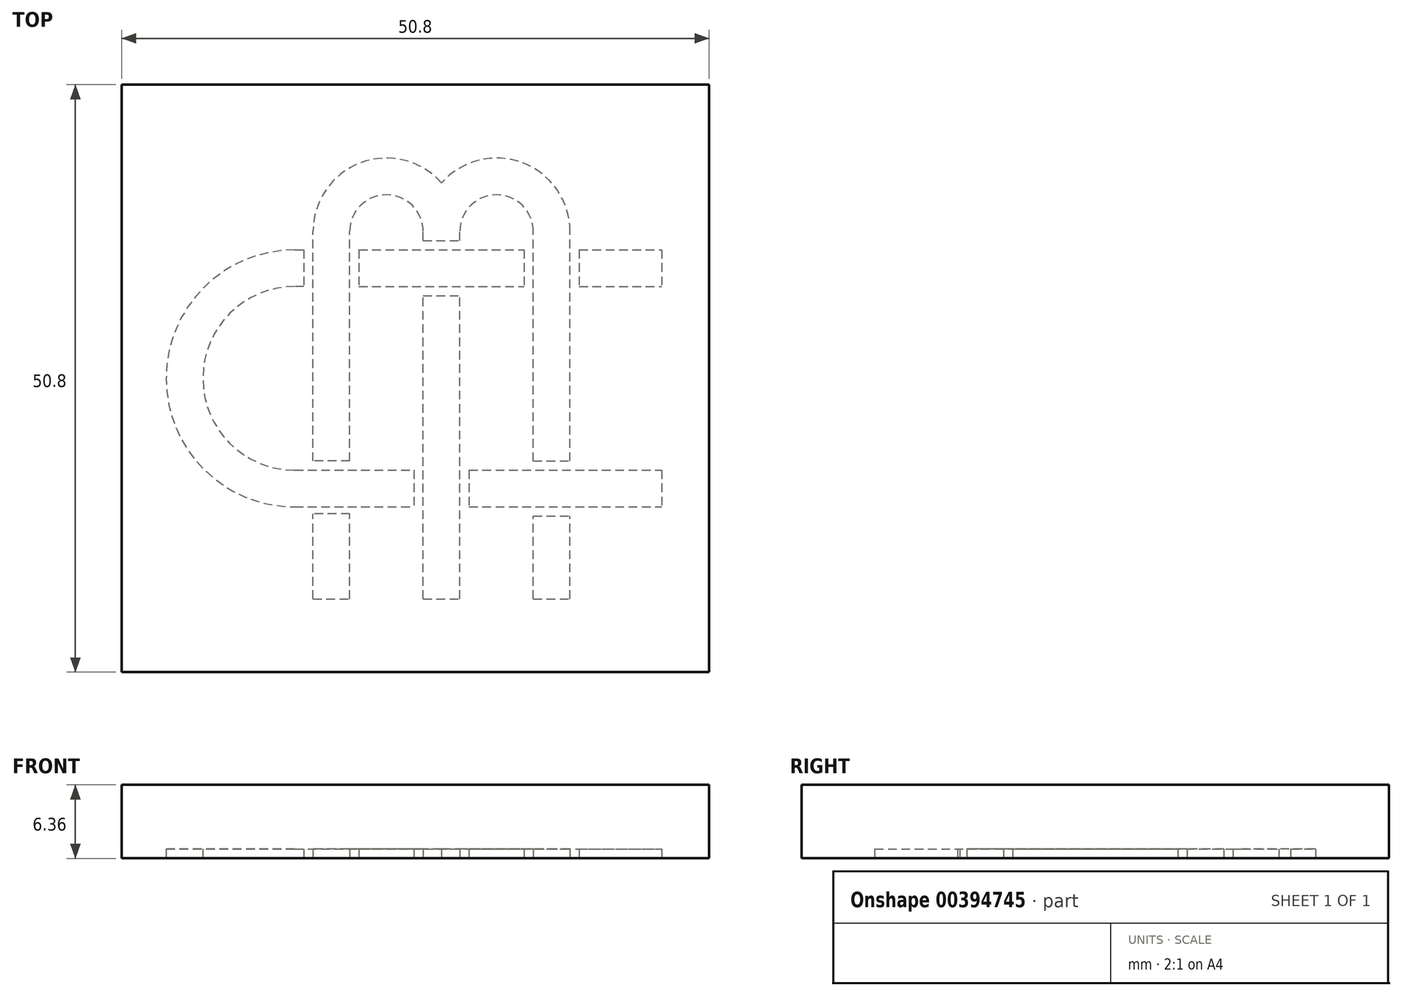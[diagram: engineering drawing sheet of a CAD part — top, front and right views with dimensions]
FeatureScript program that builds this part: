
annotation { "Feature Type Name" : "Feature", "Feature Type Description" : "" }
export const myFeature = defineFeature(function(context is Context, id is Id, definition is map)
    precondition{}
    {
        {
            var Q0;
            Q0=qCreatedBy(makeId("Top.planeOp"),FACE);
            var sketch = newSketch(context, id + "F0", { "sketchPlane" : qUnion([Q0])});
            skLineSegment(sketch, "E0.bottom", {"start": v(0, 0) * mm, "end": v(50.8, 0) * mm});
            skLineSegment(sketch, "E0.top", {"start": v(0, 50.8) * mm, "end": v(50.8, 50.8) * mm});
            skLineSegment(sketch, "E0.left", {"start": v(0, 0) * mm, "end": v(0, 50.8) * mm});
            skLineSegment(sketch, "E0.right", {"start": v(50.8, 0) * mm, "end": v(50.8, 50.8) * mm});
            skSolve(sketch);
        }
        {
            var Q0;
            Q0 = qSketchRegion(id + "F0", true);
            extrude(context, id + "F1", {"entities" : qUnion([Q0]), "depth" : 3.17 * mm});
        }
        {
            var Q0;
            Q0=makeQuery(id+"F1.opExtrude","CAP_FACE",FACE,{"disambiguationData":[OSD([sQuery(id+"F0.wireOp",EDGE,"E0.bottom"),sQuery(id+"F0.wireOp",EDGE,"E0.top"),sQuery(id+"F0.wireOp",EDGE,"E0.left"),sQuery(id+"F0.wireOp",EDGE,"E0.right")])],"isStart":false});
            var sketch = newSketch(context, id + "F2", { "sketchPlane" : qUnion([Q0])});
            skLineSegment(sketch, "E1.bottom", {"start": v(19.72, 12.7) * mm, "end": v(16.55, 12.7) * mm});
            skLineSegment(sketch, "E1.left", {"start": v(19.72, 12.7) * mm, "end": v(19.72, 13.7) * mm});
            skLineSegment(sketch, "E1.right", {"start": v(16.55, 12.7) * mm, "end": v(16.55, 13.7) * mm});
            skLineSegment(sketch, "E2", {"start": v(16.55, 12.7) * mm, "end": v(54.65, 12.7) * mm, "construction": true});
            skLineSegment(sketch, "E3.bottom", {"start": v(26.07, 12.7) * mm, "end": v(29.25, 12.7) * mm});
            skLineSegment(sketch, "E3.left", {"start": v(26.07, 12.7) * mm, "end": v(26.07, 32.6) * mm});
            skLineSegment(sketch, "E3.right", {"start": v(29.25, 12.7) * mm, "end": v(29.25, 32.6) * mm});
            skLineSegment(sketch, "E4.bottom", {"start": v(35.6, 12.7) * mm, "end": v(38.77, 12.7) * mm});
            skLineSegment(sketch, "E4.left", {"start": v(35.6, 12.7) * mm, "end": v(35.6, 13.5) * mm});
            skLineSegment(sketch, "E4.right", {"start": v(38.77, 12.7) * mm, "end": v(38.77, 13.5) * mm});
            skLineSegment(sketch, "E5.0", {"start": v(50.8, 0) * mm, "end": v(50.8, 50.8) * mm, "construction": true});
            skLineSegment(sketch, "E6", {"start": v(11.9, 41.28) * mm, "end": v(43.43, 41.28) * mm, "construction": true});
            skLineSegment(sketch, "E7", {"start": v(22.9, 41.28) * mm, "end": v(22.9, 12.7) * mm, "construction": true});
            skLineSegment(sketch, "E8", {"start": v(32.42, 41.28) * mm, "end": v(32.42, 12.7) * mm, "construction": true});
            skLineSegment(sketch, "E9", {"start": v(27.66, 41.28) * mm, "end": v(27.66, 34.87) * mm, "construction": true});
            skLineSegment(sketch, "E10", {"start": v(19.72, 38.1) * mm, "end": v(26.07, 38.1) * mm, "construction": true});
            skLineSegment(sketch, "E11", {"start": v(29.25, 38.1) * mm, "end": v(35.6, 38.1) * mm, "construction": true});
            skArc(sketch, "E12", {"start": v(19.72, 38.1) * mm, "mid": v(22.9, 41.28) * mm, "end": v(26.07, 38.1) * mm});
            skArc(sketch, "E13", {"start": v(29.25, 38.1) * mm, "mid": v(32.42, 41.28) * mm, "end": v(35.6, 38.1) * mm});
            skCircle(sketch, "E14", {"center": v(22.9, 38.1) * mm, "radius": 6.35 * mm, "construction": true});
            skCircle(sketch, "E15", {"center": v(32.42, 38.1) * mm, "radius": 6.35 * mm, "construction": true});
            skArc(sketch, "E16", {"start": v(16.55, 38.1) * mm, "mid": v(20.65, 44.04) * mm, "end": v(27.66, 42.3) * mm});
            skArc(sketch, "E17", {"start": v(38.77, 38.1) * mm, "mid": v(34.67, 44.04) * mm, "end": v(27.66, 42.3) * mm});
            skLineSegment(sketch, "E18", {"start": v(22.9, 31.75) * mm, "end": v(42, 31.75) * mm, "construction": true});
            skLineSegment(sketch, "E19", {"start": v(22.9, 31.75) * mm, "end": v(16.55, 31.75) * mm, "construction": true});
            skLineSegment(sketch, "E20.0", {"start": v(0, 50.8) * mm, "end": v(50.8, 50.8) * mm, "construction": true});
            skLineSegment(sketch, "E21", {"start": v(0, 14.29) * mm, "end": v(50.8, 14.29) * mm, "construction": true});
            skLineSegment(sketch, "E22", {"start": v(0, 36.51) * mm, "end": v(50.8, 36.51) * mm, "construction": true});
            skLineSegment(sketch, "E23", {"start": v(0, 25.4) * mm, "end": v(50.8, 25.4) * mm, "construction": true});
            skLineSegment(sketch, "E24", {"start": v(0, 33.34) * mm, "end": v(50.8, 33.34) * mm, "construction": true});
            skLineSegment(sketch, "E25", {"start": v(0, 17.46) * mm, "end": v(50.8, 17.46) * mm, "construction": true});
            skLineSegment(sketch, "E26", {"start": v(14.96, 36.51) * mm, "end": v(14.96, 33.34) * mm, "construction": true});
            skLineSegment(sketch, "E27", {"start": v(14.96, 17.46) * mm, "end": v(14.96, 14.29) * mm, "construction": true});
            skLineSegment(sketch, "E28", {"start": v(8.61, 36.51) * mm, "end": v(8.61, 14.29) * mm, "construction": true});
            skLineSegment(sketch, "E29", {"start": v(8.61, 25.4) * mm, "end": v(11.79, 25.4) * mm, "construction": true});
            skLineSegment(sketch, "E30", {"start": v(15.75, 36.51) * mm, "end": v(15.75, 33.34) * mm, "construction": true});
            skLineSegment(sketch, "E31", {"start": v(14.96, 36.51) * mm, "end": v(15.75, 36.51) * mm});
            skLineSegment(sketch, "E32", {"start": v(15.75, 33.34) * mm, "end": v(14.96, 33.34) * mm});
            skLineSegment(sketch, "E33", {"start": v(15.75, 36.51) * mm, "end": v(15.75, 33.34) * mm});
            skLineSegment(sketch, "E34", {"start": v(26.07, 32.54) * mm, "end": v(29.25, 32.54) * mm});
            skLineSegment(sketch, "E35", {"start": v(26.07, 37.3) * mm, "end": v(29.25, 37.3) * mm});
            skLineSegment(sketch, "E36.trimOffspring", {"start": v(26.07, 37.3) * mm, "end": v(26.07, 38.1) * mm});
            skLineSegment(sketch, "E37.trimOffspring", {"start": v(29.25, 37.3) * mm, "end": v(29.25, 38.1) * mm});
            skLineSegment(sketch, "E38", {"start": v(20.52, 36.51) * mm, "end": v(20.52, 33.34) * mm});
            skLineSegment(sketch, "E39", {"start": v(34.8, 36.51) * mm, "end": v(34.8, 33.34) * mm});
            skLineSegment(sketch, "E40", {"start": v(20.52, 36.51) * mm, "end": v(34.8, 36.51) * mm});
            skLineSegment(sketch, "E41", {"start": v(20.52, 33.34) * mm, "end": v(34.8, 33.34) * mm});
            skLineSegment(sketch, "E42", {"start": v(39.57, 36.51) * mm, "end": v(39.57, 33.34) * mm});
            skLineSegment(sketch, "E43", {"start": v(39.57, 36.51) * mm, "end": v(40.36, 36.51) * mm});
            skLineSegment(sketch, "E44", {"start": v(39.57, 33.34) * mm, "end": v(40.36, 33.34) * mm});
            skLineSegment(sketch, "E45", {"start": v(19.72, 18.26) * mm, "end": v(16.55, 18.26) * mm});
            skLineSegment(sketch, "E46", {"start": v(19.72, 13.7) * mm, "end": v(16.55, 13.7) * mm});
            skLineSegment(sketch, "E47.trimOffspring", {"start": v(16.55, 18.26) * mm, "end": v(16.55, 38.1) * mm});
            skLineSegment(sketch, "E48.trimOffspring", {"start": v(19.72, 18.26) * mm, "end": v(19.72, 38.1) * mm});
            skLineSegment(sketch, "E49", {"start": v(25.28, 17.46) * mm, "end": v(25.28, 14.29) * mm});
            skLineSegment(sketch, "E50", {"start": v(14.96, 17.46) * mm, "end": v(25.28, 17.46) * mm});
            skLineSegment(sketch, "E51", {"start": v(14.96, 14.29) * mm, "end": v(25.28, 14.29) * mm});
            skLineSegment(sketch, "E52", {"start": v(35.6, 18.26) * mm, "end": v(38.77, 18.26) * mm});
            skLineSegment(sketch, "E53", {"start": v(35.6, 13.5) * mm, "end": v(38.77, 13.5) * mm});
            skLineSegment(sketch, "E54.trimOffspring", {"start": v(35.6, 18.26) * mm, "end": v(35.6, 38.1) * mm});
            skLineSegment(sketch, "E55.trimOffspring", {"start": v(38.77, 18.26) * mm, "end": v(38.77, 38.1) * mm});
            skLineSegment(sketch, "E56", {"start": v(30.04, 17.46) * mm, "end": v(30.04, 14.29) * mm});
            skLineSegment(sketch, "E57", {"start": v(30.04, 17.46) * mm, "end": v(40.36, 17.46) * mm});
            skLineSegment(sketch, "E58", {"start": v(30.04, 14.29) * mm, "end": v(40.36, 14.29) * mm});
            skLineSegment(sketch, "E59", {"start": v(46.71, 14.29) * mm, "end": v(46.71, 36.51) * mm, "construction": true});
            skLineSegment(sketch, "E60", {"start": v(40.36, 36.51) * mm, "end": v(46.71, 36.51) * mm});
            skLineSegment(sketch, "E61", {"start": v(46.71, 33.34) * mm, "end": v(40.36, 33.34) * mm});
            skLineSegment(sketch, "E62", {"start": v(40.36, 17.46) * mm, "end": v(46.71, 17.46) * mm});
            skLineSegment(sketch, "E63", {"start": v(46.71, 17.46) * mm, "end": v(46.71, 14.29) * mm});
            skLineSegment(sketch, "E64", {"start": v(39.57, 36.51) * mm, "end": v(46.71, 36.51) * mm});
            skLineSegment(sketch, "E65", {"start": v(46.71, 36.51) * mm, "end": v(46.71, 33.34) * mm});
            skLineSegment(sketch, "E66.bottom", {"start": v(30.04, 17.46) * mm, "end": v(46.71, 17.46) * mm});
            skLineSegment(sketch, "E66.top", {"start": v(30.04, 17.46) * mm, "end": v(46.71, 17.46) * mm});
            skLineSegment(sketch, "E66.left", {"start": v(30.04, 17.46) * mm, "end": v(30.04, 17.46) * mm});
            skLineSegment(sketch, "E66.right", {"start": v(46.71, 17.46) * mm, "end": v(46.71, 17.46) * mm});
            skLineSegment(sketch, "E67", {"start": v(30.04, 14.29) * mm, "end": v(46.71, 14.29) * mm});
            skLineSegment(sketch, "E68.bottom", {"start": v(16.55, 12.7) * mm, "end": v(19.72, 12.7) * mm});
            skLineSegment(sketch, "E68.top", {"start": v(16.55, 6.33) * mm, "end": v(19.72, 6.33) * mm});
            skLineSegment(sketch, "E68.left", {"start": v(16.55, 12.7) * mm, "end": v(16.55, 6.33) * mm});
            skLineSegment(sketch, "E68.right", {"start": v(19.72, 12.7) * mm, "end": v(19.72, 6.33) * mm});
            skPoint(sketch, "E69.oppositeSnap0", {"position": v(18.14, 6.33) * mm});
            skLineSegment(sketch, "E69.top", {"start": v(35.6, 6.33) * mm, "end": v(38.77, 6.33) * mm});
            skLineSegment(sketch, "E69.left", {"start": v(35.6, 12.7) * mm, "end": v(35.6, 6.33) * mm});
            skLineSegment(sketch, "E69.right", {"start": v(38.77, 12.7) * mm, "end": v(38.77, 6.33) * mm});
            skLineSegment(sketch, "E70.top", {"start": v(26.07, 6.33) * mm, "end": v(29.25, 6.33) * mm});
            skLineSegment(sketch, "E70.left", {"start": v(26.07, 12.7) * mm, "end": v(26.07, 6.33) * mm});
            skLineSegment(sketch, "E70.right", {"start": v(29.25, 12.7) * mm, "end": v(29.25, 6.33) * mm});
            skLineSegment(sketch, "E71.0", {"start": v(0, 0) * mm, "end": v(50.8, 0) * mm, "construction": true});
            skLineSegment(sketch, "E72", {"start": v(14.96, 33.34) * mm, "end": v(14.96, 17.46) * mm, "construction": true});
            skArc(sketch, "E73", {"start": v(14.96, 17.46) * mm, "mid": v(7.02, 25.4) * mm, "end": v(14.96, 33.34) * mm});
            skArc(sketch, "E74", {"start": v(14.96, 14.29) * mm, "mid": v(3.85, 25.4) * mm, "end": v(14.96, 36.51) * mm});
            skLineSegment(sketch, "E75.0", {"start": v(0, 0) * mm, "end": v(0, 50.8) * mm, "construction": true});
            skSolve(sketch);
        }
        {
            var Q0;
            Q0 = qSketchRegion(id + "F2", true);
            extrude(context, id + "F3", {"entities" : qUnion([Q0]), "operationType" : NewBodyOperationType.ADD, "depth" : 0.8 * mm});
        }
        {
            var Q0;
            Q0=makeQuery(id+"F1.opExtrude","CAP_FACE",FACE,{"disambiguationData":[OSD([sQuery(id+"F0.wireOp",EDGE,"E0.bottom"),sQuery(id+"F0.wireOp",EDGE,"E0.top"),sQuery(id+"F0.wireOp",EDGE,"E0.left"),sQuery(id+"F0.wireOp",EDGE,"E0.right")])],"isStart":false});
            var sketch = newSketch(context, id + "F4", { "sketchPlane" : qUnion([Q0])});
            skLineSegment(sketch, "E76.0", {"start": v(0, 50.8) * mm, "end": v(50.8, 50.8) * mm});
            skLineSegment(sketch, "E76.1", {"start": v(0, 0) * mm, "end": v(0, 50.8) * mm});
            skLineSegment(sketch, "E76.2", {"start": v(50.8, 0) * mm, "end": v(50.8, 50.8) * mm});
            skLineSegment(sketch, "E76.3", {"start": v(0, 0) * mm, "end": v(50.8, 0) * mm});
            skSolve(sketch);
        }
        {
            var Q0;
            Q0 = qSketchRegion(id + "F4", true);
            extrude(context, id + "F5", {"entities" : qUnion([Q0]), "depth" : 25.4 * mm});
        }
        {
            var Q0;
            Q0=makeQuery(id+"F5.opExtrude","SWEPT_BODY",BODY,{"disambiguationData":[OSD([sQuery(id+"F4.wireOp",EDGE,"E76.0"),sQuery(id+"F4.wireOp",EDGE,"E76.1"),sQuery(id+"F4.wireOp",EDGE,"E76.2"),sQuery(id+"F4.wireOp",EDGE,"E76.3")])]});
            var Q1;
            Q1=makeQuery(id+"F1.opExtrude","SWEPT_BODY",BODY,{"disambiguationData":[OSD([sQuery(id+"F0.wireOp",EDGE,"E0.bottom"),sQuery(id+"F0.wireOp",EDGE,"E0.top"),sQuery(id+"F0.wireOp",EDGE,"E0.left"),sQuery(id+"F0.wireOp",EDGE,"E0.right")])]});
            booleanBodies(context, id + "F6", {"operationType" : BooleanOperationType.INTERSECTION, "tools" : qUnion([Q0, Q1])});
        }
        {
            var Q0;
            Q0=makeQuery(id+"F6.opBoolean","SPLIT",FACE,{"disambiguationData":[TD([makeQuery(id+"F3.opExtrude","SWEPT_FACE",FACE,{"disambiguationData":[OSD([sQuery(id+"F2.wireOp",EDGE,"E56")])]})])],"derivedFrom":makeQuery(id+"F5.opExtrude","CAP_FACE",FACE,{"disambiguationData":[OSD([sQuery(id+"F4.wireOp",EDGE,"E76.0"),sQuery(id+"F4.wireOp",EDGE,"E76.1"),sQuery(id+"F4.wireOp",EDGE,"E76.2"),sQuery(id+"F4.wireOp",EDGE,"E76.3")])],"isStart":true})});
            var sketch = newSketch(context, id + "F7", { "sketchPlane" : qUnion([Q0])});
            skLineSegment(sketch, "E77.bottom", {"start": v(0, 0) * mm, "end": v(50.8, 0) * mm});
            skLineSegment(sketch, "E77.top", {"start": v(0, -50.8) * mm, "end": v(50.8, -50.8) * mm});
            skLineSegment(sketch, "E77.left", {"start": v(0, 0) * mm, "end": v(0, -50.8) * mm});
            skLineSegment(sketch, "E77.right", {"start": v(50.8, 0) * mm, "end": v(50.8, -50.8) * mm});
            skSolve(sketch);
        }
        {
            var Q0;
            Q0 = qSketchRegion(id + "F7", true);
            extrude(context, id + "F8", {"entities" : qUnion([Q0]), "oppositeDirection" : true, "depth" : 6.35 * mm});
        }
        {
            var Q0;
            Q0=makeQuery(id+"F6.opBoolean","INTERSECT",BODY,{"disambiguationData":[OD(7.0)],"derivedFrom":[makeQuery(id+"F1.opExtrude","SWEPT_BODY",BODY,{"disambiguationData":[OSD([sQuery(id+"F0.wireOp",EDGE,"E0.bottom"),sQuery(id+"F0.wireOp",EDGE,"E0.top"),sQuery(id+"F0.wireOp",EDGE,"E0.left"),sQuery(id+"F0.wireOp",EDGE,"E0.right")])]}),makeQuery(id+"F5.opExtrude","SWEPT_BODY",BODY,{"disambiguationData":[OSD([sQuery(id+"F4.wireOp",EDGE,"E76.0"),sQuery(id+"F4.wireOp",EDGE,"E76.1"),sQuery(id+"F4.wireOp",EDGE,"E76.2"),sQuery(id+"F4.wireOp",EDGE,"E76.3")])]})]});
            var Q1;
            Q1=makeQuery(id+"F6.opBoolean","INTERSECT",BODY,{"disambiguationData":[OD(6.0)],"derivedFrom":[makeQuery(id+"F1.opExtrude","SWEPT_BODY",BODY,{"disambiguationData":[OSD([sQuery(id+"F0.wireOp",EDGE,"E0.bottom"),sQuery(id+"F0.wireOp",EDGE,"E0.top"),sQuery(id+"F0.wireOp",EDGE,"E0.left"),sQuery(id+"F0.wireOp",EDGE,"E0.right")])]}),makeQuery(id+"F5.opExtrude","SWEPT_BODY",BODY,{"disambiguationData":[OSD([sQuery(id+"F4.wireOp",EDGE,"E76.0"),sQuery(id+"F4.wireOp",EDGE,"E76.1"),sQuery(id+"F4.wireOp",EDGE,"E76.2"),sQuery(id+"F4.wireOp",EDGE,"E76.3")])]})]});
            var Q2;
            Q2=makeQuery(id+"F6.opBoolean","INTERSECT",BODY,{"disambiguationData":[OD(4.0)],"derivedFrom":[makeQuery(id+"F1.opExtrude","SWEPT_BODY",BODY,{"disambiguationData":[OSD([sQuery(id+"F0.wireOp",EDGE,"E0.bottom"),sQuery(id+"F0.wireOp",EDGE,"E0.top"),sQuery(id+"F0.wireOp",EDGE,"E0.left"),sQuery(id+"F0.wireOp",EDGE,"E0.right")])]}),makeQuery(id+"F5.opExtrude","SWEPT_BODY",BODY,{"disambiguationData":[OSD([sQuery(id+"F4.wireOp",EDGE,"E76.0"),sQuery(id+"F4.wireOp",EDGE,"E76.1"),sQuery(id+"F4.wireOp",EDGE,"E76.2"),sQuery(id+"F4.wireOp",EDGE,"E76.3")])]})]});
            var Q3;
            Q3=makeQuery(id+"F6.opBoolean","INTERSECT",BODY,{"disambiguationData":[OD(2.0)],"derivedFrom":[makeQuery(id+"F1.opExtrude","SWEPT_BODY",BODY,{"disambiguationData":[OSD([sQuery(id+"F0.wireOp",EDGE,"E0.bottom"),sQuery(id+"F0.wireOp",EDGE,"E0.top"),sQuery(id+"F0.wireOp",EDGE,"E0.left"),sQuery(id+"F0.wireOp",EDGE,"E0.right")])]}),makeQuery(id+"F5.opExtrude","SWEPT_BODY",BODY,{"disambiguationData":[OSD([sQuery(id+"F4.wireOp",EDGE,"E76.0"),sQuery(id+"F4.wireOp",EDGE,"E76.1"),sQuery(id+"F4.wireOp",EDGE,"E76.2"),sQuery(id+"F4.wireOp",EDGE,"E76.3")])]})]});
            var Q4;
            Q4=makeQuery(id+"F6.opBoolean","INTERSECT",BODY,{"disambiguationData":[OD(0.0)],"derivedFrom":[makeQuery(id+"F1.opExtrude","SWEPT_BODY",BODY,{"disambiguationData":[OSD([sQuery(id+"F0.wireOp",EDGE,"E0.bottom"),sQuery(id+"F0.wireOp",EDGE,"E0.top"),sQuery(id+"F0.wireOp",EDGE,"E0.left"),sQuery(id+"F0.wireOp",EDGE,"E0.right")])]}),makeQuery(id+"F5.opExtrude","SWEPT_BODY",BODY,{"disambiguationData":[OSD([sQuery(id+"F4.wireOp",EDGE,"E76.0"),sQuery(id+"F4.wireOp",EDGE,"E76.1"),sQuery(id+"F4.wireOp",EDGE,"E76.2"),sQuery(id+"F4.wireOp",EDGE,"E76.3")])]})]});
            var Q5;
            Q5=makeQuery(id+"F6.opBoolean","INTERSECT",BODY,{"disambiguationData":[OD(1.0)],"derivedFrom":[makeQuery(id+"F1.opExtrude","SWEPT_BODY",BODY,{"disambiguationData":[OSD([sQuery(id+"F0.wireOp",EDGE,"E0.bottom"),sQuery(id+"F0.wireOp",EDGE,"E0.top"),sQuery(id+"F0.wireOp",EDGE,"E0.left"),sQuery(id+"F0.wireOp",EDGE,"E0.right")])]}),makeQuery(id+"F5.opExtrude","SWEPT_BODY",BODY,{"disambiguationData":[OSD([sQuery(id+"F4.wireOp",EDGE,"E76.0"),sQuery(id+"F4.wireOp",EDGE,"E76.1"),sQuery(id+"F4.wireOp",EDGE,"E76.2"),sQuery(id+"F4.wireOp",EDGE,"E76.3")])]})]});
            var Q6;
            Q6=makeQuery(id+"F6.opBoolean","INTERSECT",BODY,{"disambiguationData":[OD(5.0)],"derivedFrom":[makeQuery(id+"F1.opExtrude","SWEPT_BODY",BODY,{"disambiguationData":[OSD([sQuery(id+"F0.wireOp",EDGE,"E0.bottom"),sQuery(id+"F0.wireOp",EDGE,"E0.top"),sQuery(id+"F0.wireOp",EDGE,"E0.left"),sQuery(id+"F0.wireOp",EDGE,"E0.right")])]}),makeQuery(id+"F5.opExtrude","SWEPT_BODY",BODY,{"disambiguationData":[OSD([sQuery(id+"F4.wireOp",EDGE,"E76.0"),sQuery(id+"F4.wireOp",EDGE,"E76.1"),sQuery(id+"F4.wireOp",EDGE,"E76.2"),sQuery(id+"F4.wireOp",EDGE,"E76.3")])]})]});
            var Q7;
            Q7=makeQuery(id+"F6.opBoolean","INTERSECT",BODY,{"disambiguationData":[OD(3.0)],"derivedFrom":[makeQuery(id+"F1.opExtrude","SWEPT_BODY",BODY,{"disambiguationData":[OSD([sQuery(id+"F0.wireOp",EDGE,"E0.bottom"),sQuery(id+"F0.wireOp",EDGE,"E0.top"),sQuery(id+"F0.wireOp",EDGE,"E0.left"),sQuery(id+"F0.wireOp",EDGE,"E0.right")])]}),makeQuery(id+"F5.opExtrude","SWEPT_BODY",BODY,{"disambiguationData":[OSD([sQuery(id+"F4.wireOp",EDGE,"E76.0"),sQuery(id+"F4.wireOp",EDGE,"E76.1"),sQuery(id+"F4.wireOp",EDGE,"E76.2"),sQuery(id+"F4.wireOp",EDGE,"E76.3")])]})]});
            var Q8;
            Q8=makeQuery(id+"F8.opExtrude","SWEPT_BODY",BODY,{"disambiguationData":[OSD([sQuery(id+"F7.wireOp",EDGE,"E77.bottom"),sQuery(id+"F7.wireOp",EDGE,"E77.top"),sQuery(id+"F7.wireOp",EDGE,"E77.left"),sQuery(id+"F7.wireOp",EDGE,"E77.right")])]});
            booleanBodies(context, id + "F9", {"operationType" : BooleanOperationType.SUBTRACTION, "tools" : qUnion([Q0, Q1, Q2, Q3, Q4, Q5, Q6, Q7]), "targets" : qUnion([Q8])});
        }
    });
